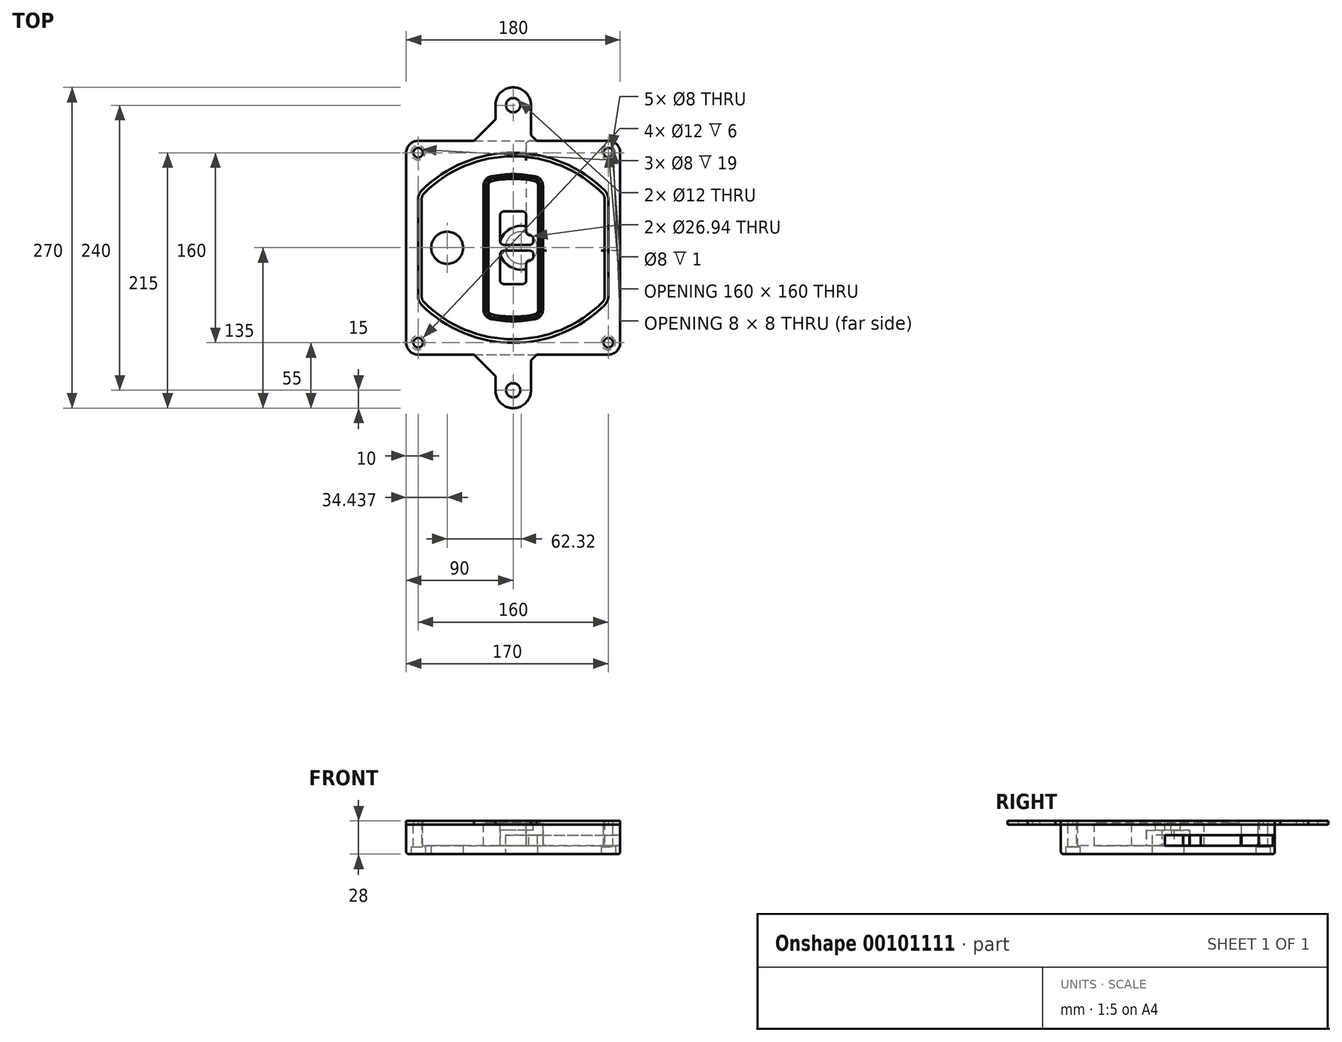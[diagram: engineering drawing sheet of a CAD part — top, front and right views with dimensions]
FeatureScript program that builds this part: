
annotation { "Feature Type Name" : "Feature", "Feature Type Description" : "" }
export const myFeature = defineFeature(function(context is Context, id is Id, definition is map)
    precondition{}
    {
        {
            var Q0;
            Q0=qCreatedBy(makeId("Top.planeOp"),FACE);
            var sketch = newSketch(context, id + "F0", { "sketchPlane" : qUnion([Q0])});
            skPoint(sketch, "E0.rect.middle", {"position": v(0, 0) * mm});
            skLineSegment(sketch, "E1.bottom", {"start": v(-80, -90) * mm, "end": v(80, -90) * mm});
            skLineSegment(sketch, "E1.top", {"start": v(-80, 90) * mm, "end": v(80, 90) * mm});
            skLineSegment(sketch, "E1.left", {"start": v(-90, -80) * mm, "end": v(-90, 80) * mm});
            skLineSegment(sketch, "E1.right", {"start": v(90, -80) * mm, "end": v(90, 80) * mm});
            skLineSegment(sketch, "E2", {"start": v(-90, 90) * mm, "end": v(90, -90) * mm, "construction": true});
            skLineSegment(sketch, "E3", {"start": v(90, 90) * mm, "end": v(-90, -90) * mm, "construction": true});
            skCircle(sketch, "E4", {"center": v(-80, 80) * mm, "radius": 4 * mm});
            skCircle(sketch, "E5", {"center": v(80, 80) * mm, "radius": 4 * mm});
            skCircle(sketch, "E6", {"center": v(80, -80) * mm, "radius": 4 * mm});
            skCircle(sketch, "E7", {"center": v(-80, -80) * mm, "radius": 4 * mm});
            skLineSegment(sketch, "E8", {"start": v(-80, 80) * mm, "end": v(80, 80) * mm, "construction": true});
            skLineSegment(sketch, "E9", {"start": v(80, 80) * mm, "end": v(80, -80) * mm, "construction": true});
            skLineSegment(sketch, "E10", {"start": v(80, -80) * mm, "end": v(-80, -80) * mm, "construction": true});
            skLineSegment(sketch, "E11", {"start": v(-80, -80) * mm, "end": v(-80, 80) * mm, "construction": true});
            skLineSegment(sketch, "E12", {"start": v(-80, 40.98) * mm, "end": v(-80, -40.98) * mm});
            skLineSegment(sketch, "E13", {"start": v(80, 40.98) * mm, "end": v(80, -40.98) * mm});
            skArc(sketch, "E14", {"start": v(77.08, 48.04) * mm, "mid": v(0, 80) * mm, "end": v(-77.08, 48.04) * mm});
            skArc(sketch, "E15", {"start": v(-77.08, -48.04) * mm, "mid": v(0, -80) * mm, "end": v(77.08, -48.04) * mm});
            skLineSegment(sketch, "E16", {"start": v(-80, 0) * mm, "end": v(80, 0) * mm, "construction": true});
            skPoint(sketch, "E17.visualSharp", {"position": v(-80, -45) * mm});
            skArc(sketch, "E17.filletArc", {"start": v(-80, -40.98) * mm, "mid": v(-79.24, -44.8) * mm, "end": v(-77.08, -48.04) * mm});
            skPoint(sketch, "E18.visualSharp", {"position": v(-80, 45) * mm});
            skArc(sketch, "E18.filletArc", {"start": v(-77.08, 48.04) * mm, "mid": v(-79.24, 44.8) * mm, "end": v(-80, 40.98) * mm});
            skPoint(sketch, "E19.visualSharp", {"position": v(80, 45) * mm});
            skArc(sketch, "E19.filletArc", {"start": v(80, 40.98) * mm, "mid": v(79.24, 44.8) * mm, "end": v(77.08, 48.04) * mm});
            skPoint(sketch, "E20.visualSharp", {"position": v(80, -45) * mm});
            skArc(sketch, "E20.filletArc", {"start": v(77.08, -48.04) * mm, "mid": v(79.24, -44.8) * mm, "end": v(80, -40.98) * mm});
            skPoint(sketch, "E21.visualSharp", {"position": v(-90, 90) * mm});
            skArc(sketch, "E21.filletArc", {"start": v(-80, 90) * mm, "mid": v(-87.07, 87.07) * mm, "end": v(-90, 80) * mm});
            skPoint(sketch, "E22.visualSharp", {"position": v(90, 90) * mm});
            skArc(sketch, "E22.filletArc", {"start": v(90, 80) * mm, "mid": v(87.07, 87.07) * mm, "end": v(80, 90) * mm});
            skPoint(sketch, "E23.visualSharp", {"position": v(90, -90) * mm});
            skArc(sketch, "E23.filletArc", {"start": v(80, -90) * mm, "mid": v(87.07, -87.07) * mm, "end": v(90, -80) * mm});
            skPoint(sketch, "E24.visualSharp", {"position": v(-90, -90) * mm});
            skArc(sketch, "E24.filletArc", {"start": v(-90, -80) * mm, "mid": v(-87.07, -87.07) * mm, "end": v(-80, -90) * mm});
            skArc(sketch, "E25.0", {"start": v(77, 40.98) * mm, "mid": v(76.47, 43.65) * mm, "end": v(74.95, 45.92) * mm});
            skLineSegment(sketch, "E25.1", {"start": v(77, 40.98) * mm, "end": v(77, -40.98) * mm});
            skArc(sketch, "E25.2", {"start": v(74.95, -45.92) * mm, "mid": v(76.47, -43.65) * mm, "end": v(77, -40.98) * mm});
            skArc(sketch, "E25.3", {"start": v(-74.95, -45.92) * mm, "mid": v(0, -77) * mm, "end": v(74.95, -45.92) * mm});
            skArc(sketch, "E25.4", {"start": v(-77, -40.98) * mm, "mid": v(-76.47, -43.65) * mm, "end": v(-74.95, -45.92) * mm});
            skArc(sketch, "E25.5", {"start": v(74.95, 45.92) * mm, "mid": v(0, 77) * mm, "end": v(-74.95, 45.92) * mm});
            skLineSegment(sketch, "E25.6", {"start": v(-77, 40.98) * mm, "end": v(-77, -40.98) * mm});
            skArc(sketch, "E25.7", {"start": v(-74.95, 45.92) * mm, "mid": v(-76.47, 43.65) * mm, "end": v(-77, 40.98) * mm});
            skArc(sketch, "E26.0", {"start": v(-79.9, 50.87) * mm, "mid": v(-82.94, 46.33) * mm, "end": v(-84, 40.98) * mm});
            skArc(sketch, "E26.1", {"start": v(79.9, 50.87) * mm, "mid": v(0, 84) * mm, "end": v(-79.9, 50.87) * mm});
            skArc(sketch, "E26.2", {"start": v(84, 40.98) * mm, "mid": v(82.94, 46.33) * mm, "end": v(79.9, 50.87) * mm});
            skLineSegment(sketch, "E26.3", {"start": v(84, 40.98) * mm, "end": v(84, -40.98) * mm});
            skArc(sketch, "E26.4", {"start": v(79.9, -50.87) * mm, "mid": v(82.94, -46.33) * mm, "end": v(84, -40.98) * mm});
            skLineSegment(sketch, "E26.5", {"start": v(-84, 40.98) * mm, "end": v(-84, -40.98) * mm});
            skArc(sketch, "E26.6", {"start": v(-79.9, -50.87) * mm, "mid": v(0, -84) * mm, "end": v(79.9, -50.87) * mm});
            skArc(sketch, "E26.7", {"start": v(-84, -40.98) * mm, "mid": v(-82.94, -46.33) * mm, "end": v(-79.9, -50.87) * mm});
            skSolve(sketch);
        }
        {
            var Q0;
            Q0=makeQuery(id+"F0.imprint","IMPRINT",FACE,{"disambiguationData":[TD([[makeQuery(id+"F0.imprint","IMPRINT",EDGE,{"derivedFrom":sQuery(id+"F0.wireOp",EDGE,"E1.bottom")}),1.0]])]});
            var Q1;
            Q1=makeQuery(id+"F0.imprint","IMPRINT",FACE,{"disambiguationData":[TD([[makeQuery(id+"F0.imprint","IMPRINT",EDGE,{"derivedFrom":sQuery(id+"F0.wireOp",EDGE,"E12")}),1.0]])]});
            var Q2;
            Q2=makeQuery(id+"F0.imprint","IMPRINT",FACE,{"disambiguationData":[TD([[makeQuery(id+"F0.imprint","IMPRINT",EDGE,{"derivedFrom":sQuery(id+"F0.wireOp",EDGE,"E25.0")}),1.0]])]});
            var Q3;
            Q3=makeQuery(id+"F0.imprint","IMPRINT",FACE,{"disambiguationData":[TD([[makeQuery(id+"F0.imprint","IMPRINT",EDGE,{"derivedFrom":sQuery(id+"F0.wireOp",EDGE,"E12")}),-1.0]])]});
            extrude(context, id + "F1", {"entities" : qUnion([Q0, Q1, Q2, Q3]), "oppositeDirection" : true, "depth" : 25 * mm});
        }
        {
            var Q0;
            Q0=makeQuery(id+"F0.imprint","IMPRINT",FACE,{"disambiguationData":[TD([[makeQuery(id+"F0.imprint","IMPRINT",EDGE,{"derivedFrom":sQuery(id+"F0.wireOp",EDGE,"E12")}),1.0]])]});
            extrude(context, id + "F2", {"entities" : qUnion([Q0]), "operationType" : NewBodyOperationType.ADD, "depth" : 3 * mm});
        }
        {
            var Q0;
            Q0=makeQuery(id+"F0.imprint","IMPRINT",FACE,{"disambiguationData":[TD([[makeQuery(id+"F0.imprint","IMPRINT",EDGE,{"derivedFrom":sQuery(id+"F0.wireOp",EDGE,"E25.0")}),1.0]])]});
            extrude(context, id + "F3", {"entities" : qUnion([Q0]), "operationType" : NewBodyOperationType.REMOVE, "oppositeDirection" : true, "depth" : 18 * mm});
        }
        {
            var Q0;
            Q0=makeQuery(id+"F2.opExtrude","CAP_FACE",FACE,{"disambiguationData":[OSD([sQuery(id+"F0.wireOp",EDGE,"E12"),sQuery(id+"F0.wireOp",EDGE,"E13"),sQuery(id+"F0.wireOp",EDGE,"E14"),sQuery(id+"F0.wireOp",EDGE,"E15"),sQuery(id+"F0.wireOp",EDGE,"E17.filletArc"),sQuery(id+"F0.wireOp",EDGE,"E18.filletArc"),sQuery(id+"F0.wireOp",EDGE,"E19.filletArc"),sQuery(id+"F0.wireOp",EDGE,"E20.filletArc"),sQuery(id+"F0.wireOp",EDGE,"E25.0"),sQuery(id+"F0.wireOp",EDGE,"E25.1"),sQuery(id+"F0.wireOp",EDGE,"E25.2"),sQuery(id+"F0.wireOp",EDGE,"E25.3"),sQuery(id+"F0.wireOp",EDGE,"E25.4"),sQuery(id+"F0.wireOp",EDGE,"E25.5"),sQuery(id+"F0.wireOp",EDGE,"E25.6"),sQuery(id+"F0.wireOp",EDGE,"E25.7")])],"isStart":false});
            var sketch = newSketch(context, id + "F4", { "sketchPlane" : qUnion([Q0])});
            skArc(sketch, "E27.0", {"start": v(-18.64, -60.07) * mm, "mid": v(0, -62) * mm, "end": v(18.64, -60.07) * mm});
            skArc(sketch, "E28.0", {"start": v(18.64, 60.07) * mm, "mid": v(0, 62) * mm, "end": v(-18.64, 60.07) * mm});
            skLineSegment(sketch, "E29", {"start": v(-25, 52.24) * mm, "end": v(-25, -52.24) * mm});
            skLineSegment(sketch, "E30", {"start": v(25, 52.24) * mm, "end": v(25, -52.24) * mm});
            skLineSegment(sketch, "E31", {"start": v(-25, 58.5) * mm, "end": v(25, 58.5) * mm, "construction": true});
            skLineSegment(sketch, "E32", {"start": v(-25, -58.5) * mm, "end": v(25, -58.5) * mm, "construction": true});
            skPoint(sketch, "E33.visualSharp", {"position": v(-25, 58.5) * mm});
            skArc(sketch, "E33.filletArc", {"start": v(-18.64, 60.07) * mm, "mid": v(-23.2, 57.28) * mm, "end": v(-25, 52.24) * mm});
            skPoint(sketch, "E34.visualSharp", {"position": v(25, 58.5) * mm});
            skArc(sketch, "E34.filletArc", {"start": v(25, 52.24) * mm, "mid": v(23.2, 57.28) * mm, "end": v(18.64, 60.07) * mm});
            skPoint(sketch, "E35.visualSharp", {"position": v(25, -58.5) * mm});
            skArc(sketch, "E35.filletArc", {"start": v(18.64, -60.07) * mm, "mid": v(23.2, -57.28) * mm, "end": v(25, -52.24) * mm});
            skPoint(sketch, "E36.visualSharp", {"position": v(-25, -58.5) * mm});
            skArc(sketch, "E36.filletArc", {"start": v(-25, -52.24) * mm, "mid": v(-23.2, -57.28) * mm, "end": v(-18.64, -60.07) * mm});
            skArc(sketch, "E37.0", {"start": v(74.95, 45.92) * mm, "mid": v(0, 77) * mm, "end": v(-74.95, 45.92) * mm});
            skArc(sketch, "E37.1", {"start": v(-74.95, 45.92) * mm, "mid": v(-76.47, 43.65) * mm, "end": v(-77, 40.98) * mm});
            skLineSegment(sketch, "E37.2", {"start": v(-77, 40.98) * mm, "end": v(-77, -40.98) * mm});
            skArc(sketch, "E37.3", {"start": v(-77, -40.98) * mm, "mid": v(-76.47, -43.65) * mm, "end": v(-74.95, -45.92) * mm});
            skArc(sketch, "E37.4", {"start": v(-74.95, -45.92) * mm, "mid": v(0, -77) * mm, "end": v(74.95, -45.92) * mm});
            skArc(sketch, "E37.5", {"start": v(74.95, -45.92) * mm, "mid": v(76.47, -43.65) * mm, "end": v(77, -40.98) * mm});
            skLineSegment(sketch, "E37.6", {"start": v(77, 40.98) * mm, "end": v(77, -40.98) * mm});
            skArc(sketch, "E37.7", {"start": v(77, 40.98) * mm, "mid": v(76.47, 43.65) * mm, "end": v(74.95, 45.92) * mm});
            skLineSegment(sketch, "E38.0", {"start": v(23, 52.24) * mm, "end": v(23, -52.24) * mm});
            skArc(sketch, "E38.1", {"start": v(18.23, -58.11) * mm, "mid": v(21.66, -56.02) * mm, "end": v(23, -52.24) * mm});
            skArc(sketch, "E38.2", {"start": v(-18.23, -58.11) * mm, "mid": v(0, -60) * mm, "end": v(18.23, -58.11) * mm});
            skArc(sketch, "E38.3", {"start": v(-23, -52.24) * mm, "mid": v(-21.66, -56.02) * mm, "end": v(-18.23, -58.11) * mm});
            skLineSegment(sketch, "E38.4", {"start": v(-23, 52.24) * mm, "end": v(-23, -52.24) * mm});
            skArc(sketch, "E38.5", {"start": v(23, 52.24) * mm, "mid": v(21.66, 56.02) * mm, "end": v(18.23, 58.11) * mm});
            skArc(sketch, "E38.6", {"start": v(-18.23, 58.11) * mm, "mid": v(-21.66, 56.02) * mm, "end": v(-23, 52.24) * mm});
            skArc(sketch, "E38.7", {"start": v(18.23, 58.11) * mm, "mid": v(0, 60) * mm, "end": v(-18.23, 58.11) * mm});
            skArc(sketch, "E39.0", {"start": v(21, 52.24) * mm, "mid": v(20.1, 54.76) * mm, "end": v(17.82, 56.15) * mm});
            skLineSegment(sketch, "E39.1", {"start": v(21, 52.24) * mm, "end": v(21, -52.24) * mm});
            skArc(sketch, "E39.2", {"start": v(17.82, -56.15) * mm, "mid": v(20.1, -54.76) * mm, "end": v(21, -52.24) * mm});
            skArc(sketch, "E39.3", {"start": v(-17.82, -56.15) * mm, "mid": v(0, -58) * mm, "end": v(17.82, -56.15) * mm});
            skArc(sketch, "E39.4", {"start": v(-21, -52.24) * mm, "mid": v(-20.1, -54.76) * mm, "end": v(-17.82, -56.15) * mm});
            skArc(sketch, "E39.5", {"start": v(17.82, 56.15) * mm, "mid": v(0, 58) * mm, "end": v(-17.82, 56.15) * mm});
            skLineSegment(sketch, "E39.6", {"start": v(-21, 52.24) * mm, "end": v(-21, -52.24) * mm});
            skArc(sketch, "E39.7", {"start": v(-17.82, 56.15) * mm, "mid": v(-20.1, 54.76) * mm, "end": v(-21, 52.24) * mm});
            skLineSegment(sketch, "E40", {"start": v(-25, 0) * mm, "end": v(25, 0) * mm, "construction": true});
            skLineSegment(sketch, "E41", {"start": v(-11, 5.5) * mm, "end": v(-11, 27.5) * mm});
            skLineSegment(sketch, "E42", {"start": v(-8, 30.5) * mm, "end": v(8, 30.5) * mm});
            skLineSegment(sketch, "E43", {"start": v(11, 27.5) * mm, "end": v(11, 13.5) * mm});
            skLineSegment(sketch, "E44", {"start": v(14, 10.5) * mm, "end": v(14, 10.5) * mm});
            skLineSegment(sketch, "E45", {"start": v(17, 7.5) * mm, "end": v(17, 5.5) * mm});
            skLineSegment(sketch, "E46", {"start": v(14, 2.5) * mm, "end": v(-8, 2.5) * mm});
            skPoint(sketch, "E47.visualSharp", {"position": v(-11, 30.5) * mm});
            skArc(sketch, "E47.filletArc", {"start": v(-8, 30.5) * mm, "mid": v(-10.12, 29.62) * mm, "end": v(-11, 27.5) * mm});
            skPoint(sketch, "E48.visualSharp", {"position": v(11, 30.5) * mm});
            skArc(sketch, "E48.filletArc", {"start": v(11, 27.5) * mm, "mid": v(10.12, 29.62) * mm, "end": v(8, 30.5) * mm});
            skPoint(sketch, "E49.visualSharp", {"position": v(11, 10.5) * mm});
            skArc(sketch, "E49.filletArc", {"start": v(11, 13.5) * mm, "mid": v(11.88, 11.38) * mm, "end": v(14, 10.5) * mm});
            skPoint(sketch, "E50.visualSharp", {"position": v(17, 10.5) * mm});
            skArc(sketch, "E50.filletArc", {"start": v(17, 7.5) * mm, "mid": v(16.12, 9.62) * mm, "end": v(14, 10.5) * mm});
            skPoint(sketch, "E51.visualSharp", {"position": v(17, 2.5) * mm});
            skArc(sketch, "E51.filletArc", {"start": v(14, 2.5) * mm, "mid": v(16.12, 3.38) * mm, "end": v(17, 5.5) * mm});
            skPoint(sketch, "E52.visualSharp", {"position": v(-11, 2.5) * mm});
            skArc(sketch, "E52.filletArc", {"start": v(-11, 5.5) * mm, "mid": v(-10.12, 3.38) * mm, "end": v(-8, 2.5) * mm});
            skLineSegment(sketch, "E53.0.MirrorCS", {"start": v(14, -2.5) * mm, "end": v(-8, -2.5) * mm});
            skArc(sketch, "E54.0.MirrorCS", {"start": v(-11, -5.5) * mm, "mid": v(-10.12, -3.38) * mm, "end": v(-8, -2.5) * mm});
            skLineSegment(sketch, "E55.0.MirrorCS", {"start": v(-11, -5.5) * mm, "end": v(-11, -27.5) * mm});
            skArc(sketch, "E56.0.MirrorCS", {"start": v(-8, -30.5) * mm, "mid": v(-10.12, -29.62) * mm, "end": v(-11, -27.5) * mm});
            skLineSegment(sketch, "E57.0.MirrorCS", {"start": v(-8, -30.5) * mm, "end": v(8, -30.5) * mm});
            skArc(sketch, "E58.0.MirrorCS", {"start": v(11, -27.5) * mm, "mid": v(10.12, -29.62) * mm, "end": v(8, -30.5) * mm});
            skLineSegment(sketch, "E59.0.MirrorCS", {"start": v(11, -27.5) * mm, "end": v(11, -13.5) * mm});
            skArc(sketch, "E60.0.MirrorCS", {"start": v(11, -13.5) * mm, "mid": v(11.88, -11.38) * mm, "end": v(14, -10.5) * mm});
            skArc(sketch, "E61.0.MirrorCS", {"start": v(17, -7.5) * mm, "mid": v(16.12, -9.62) * mm, "end": v(14, -10.5) * mm});
            skLineSegment(sketch, "E62.0.MirrorCS", {"start": v(17, -7.5) * mm, "end": v(17, -5.5) * mm});
            skArc(sketch, "E63.0.MirrorCS", {"start": v(14, -2.5) * mm, "mid": v(16.12, -3.38) * mm, "end": v(17, -5.5) * mm});
            skSolve(sketch);
        }
        {
            var Q0;
            Q0=makeQuery(id+"F4.imprint","IMPRINT",FACE,{"disambiguationData":[TD([[makeQuery(id+"F4.imprint","IMPRINT",EDGE,{"derivedFrom":sQuery(id+"F4.wireOp",EDGE,"E27.0")}),1.0]])]});
            var Q1;
            Q1=makeQuery(id+"F4.imprint","IMPRINT",FACE,{"disambiguationData":[TD([[makeQuery(id+"F4.imprint","IMPRINT",EDGE,{"derivedFrom":sQuery(id+"F4.wireOp",EDGE,"E38.0")}),-1.0]])]});
            var Q2;
            Q2=makeQuery(id+"F4.imprint","IMPRINT",FACE,{"disambiguationData":[TD([[makeQuery(id+"F4.imprint","IMPRINT",EDGE,{"derivedFrom":sQuery(id+"F4.wireOp",EDGE,"E39.0")}),1.0]])]});
            extrude(context, id + "F5", {"entities" : qUnion([Q0, Q1, Q2]), "operationType" : NewBodyOperationType.ADD, "endBound" : BoundingType.UP_TO_NEXT, "oppositeDirection" : true, "depth" : 25 * mm});
        }
        {
            var Q0;
            Q0=makeQuery(id+"F4.imprint","IMPRINT",FACE,{"disambiguationData":[TD([[makeQuery(id+"F4.imprint","IMPRINT",EDGE,{"derivedFrom":sQuery(id+"F4.wireOp",EDGE,"E38.0")}),-1.0]])]});
            extrude(context, id + "F6", {"entities" : qUnion([Q0]), "operationType" : NewBodyOperationType.REMOVE, "oppositeDirection" : true, "depth" : 2 * mm});
        }
        {
            var Q0;
            Q0=makeQuery(id+"F1.opExtrude","CAP_FACE",FACE,{"disambiguationData":[OSD([sQuery(id+"F0.wireOp",EDGE,"E1.bottom"),sQuery(id+"F0.wireOp",EDGE,"E1.top"),sQuery(id+"F0.wireOp",EDGE,"E1.left"),sQuery(id+"F0.wireOp",EDGE,"E1.right"),sQuery(id+"F0.wireOp",EDGE,"E4"),sQuery(id+"F0.wireOp",EDGE,"E5"),sQuery(id+"F0.wireOp",EDGE,"E6"),sQuery(id+"F0.wireOp",EDGE,"E7"),sQuery(id+"F0.wireOp",EDGE,"E21.filletArc"),sQuery(id+"F0.wireOp",EDGE,"E22.filletArc"),sQuery(id+"F0.wireOp",EDGE,"E23.filletArc"),sQuery(id+"F0.wireOp",EDGE,"E24.filletArc")])],"isStart":false});
            var sketch = newSketch(context, id + "F7", { "sketchPlane" : qUnion([Q0])});
            skCircle(sketch, "E64", {"center": v(6.76, 0) * mm, "radius": 13.47 * mm});
            skCircle(sketch, "E65", {"center": v(-55.56, 0) * mm, "radius": 13.47 * mm});
            skLineSegment(sketch, "E66", {"start": v(90, 0) * mm, "end": v(-90, 0) * mm});
            skCircle(sketch, "E67", {"center": v(6.76, 0) * mm, "radius": 18.47 * mm});
            skCircle(sketch, "E68", {"center": v(80, -80) * mm, "radius": 6 * mm});
            skCircle(sketch, "E69", {"center": v(-80, -80) * mm, "radius": 6 * mm});
            skCircle(sketch, "E70", {"center": v(-80, 80) * mm, "radius": 6 * mm});
            skCircle(sketch, "E71", {"center": v(80, 80) * mm, "radius": 6 * mm});
            skSolve(sketch);
        }
        {
            var Q0;
            {var subQ1=sQuery(id+"F7.wireOp",EDGE,"E66");var subQ4=sQuery(id+"F7.wireOp",EDGE,"E64");var subQ6=makeQuery(id+"F7.imprint","INTERSECT",VERTEX,{"disambiguationData":[OD(0.0)],"derivedFrom":[subQ4,subQ1]});Q0=makeQuery(id+"F7.imprint","IMPRINT",FACE,{"disambiguationData":[TD([[makeQuery(id+"F7.imprint","IMPRINT",EDGE,{"disambiguationData":[TD([[subQ6,-1.0]])],"derivedFrom":subQ4}),-1.0]])]});}
            var Q1;
            {var subQ0=sQuery(id+"F7.wireOp",EDGE,"E66");var subQ1=sQuery(id+"F7.wireOp",EDGE,"E64");var subQ3=makeQuery(id+"F7.imprint","INTERSECT",VERTEX,{"disambiguationData":[OD(0.0)],"derivedFrom":[subQ1,subQ0]});Q1=makeQuery(id+"F7.imprint","IMPRINT",FACE,{"disambiguationData":[TD([[makeQuery(id+"F7.imprint","IMPRINT",EDGE,{"disambiguationData":[TD([[subQ3,-1.0]])],"derivedFrom":subQ1}),1.0]])]});}
            var Q2;
            {var subQ0=sQuery(id+"F7.wireOp",EDGE,"E66");var subQ1=sQuery(id+"F7.wireOp",EDGE,"E64");var subQ3=makeQuery(id+"F7.imprint","INTERSECT",VERTEX,{"disambiguationData":[OD(0.0)],"derivedFrom":[subQ1,subQ0]});Q2=makeQuery(id+"F7.imprint","IMPRINT",FACE,{"disambiguationData":[TD([[makeQuery(id+"F7.imprint","IMPRINT",EDGE,{"disambiguationData":[TD([[subQ3,1.0]])],"derivedFrom":subQ1}),1.0]])]});}
            var Q3;
            {var subQ1=sQuery(id+"F7.wireOp",EDGE,"E66");var subQ4=sQuery(id+"F7.wireOp",EDGE,"E64");var subQ6=makeQuery(id+"F7.imprint","INTERSECT",VERTEX,{"disambiguationData":[OD(0.0)],"derivedFrom":[subQ4,subQ1]});Q3=makeQuery(id+"F7.imprint","IMPRINT",FACE,{"disambiguationData":[TD([[makeQuery(id+"F7.imprint","IMPRINT",EDGE,{"disambiguationData":[TD([[subQ6,1.0]])],"derivedFrom":subQ4}),-1.0]])]});}
            extrude(context, id + "F8", {"entities" : qUnion([Q0, Q1, Q2, Q3]), "operationType" : NewBodyOperationType.ADD, "oppositeDirection" : true, "depth" : 20 * mm});
        }
        {
            var Q0;
            {var subQ0=sQuery(id+"F7.wireOp",EDGE,"E66");var subQ1=sQuery(id+"F7.wireOp",EDGE,"E64");var subQ3=makeQuery(id+"F7.imprint","INTERSECT",VERTEX,{"disambiguationData":[OD(0.0)],"derivedFrom":[subQ1,subQ0]});Q0=makeQuery(id+"F7.imprint","IMPRINT",FACE,{"disambiguationData":[TD([[makeQuery(id+"F7.imprint","IMPRINT",EDGE,{"disambiguationData":[TD([[subQ3,-1.0]])],"derivedFrom":subQ1}),1.0]])]});}
            var Q1;
            {var subQ0=sQuery(id+"F7.wireOp",EDGE,"E66");var subQ1=sQuery(id+"F7.wireOp",EDGE,"E64");var subQ3=makeQuery(id+"F7.imprint","INTERSECT",VERTEX,{"disambiguationData":[OD(0.0)],"derivedFrom":[subQ1,subQ0]});Q1=makeQuery(id+"F7.imprint","IMPRINT",FACE,{"disambiguationData":[TD([[makeQuery(id+"F7.imprint","IMPRINT",EDGE,{"disambiguationData":[TD([[subQ3,1.0]])],"derivedFrom":subQ1}),1.0]])]});}
            extrude(context, id + "F9", {"entities" : qUnion([Q0, Q1]), "operationType" : NewBodyOperationType.REMOVE, "oppositeDirection" : true, "depth" : 16 * mm});
        }
        {
            var Q0;
            {var subQ0=sQuery(id+"F7.wireOp",EDGE,"E66");var subQ1=sQuery(id+"F7.wireOp",EDGE,"E65");var subQ3=makeQuery(id+"F7.imprint","INTERSECT",VERTEX,{"disambiguationData":[OD(0.0)],"derivedFrom":[subQ1,subQ0]});Q0=makeQuery(id+"F7.imprint","IMPRINT",FACE,{"disambiguationData":[TD([[makeQuery(id+"F7.imprint","IMPRINT",EDGE,{"disambiguationData":[TD([[subQ3,-1.0]])],"derivedFrom":subQ1}),1.0]])]});}
            var Q1;
            {var subQ0=sQuery(id+"F7.wireOp",EDGE,"E66");var subQ1=sQuery(id+"F7.wireOp",EDGE,"E65");var subQ3=makeQuery(id+"F7.imprint","INTERSECT",VERTEX,{"disambiguationData":[OD(0.0)],"derivedFrom":[subQ1,subQ0]});Q1=makeQuery(id+"F7.imprint","IMPRINT",FACE,{"disambiguationData":[TD([[makeQuery(id+"F7.imprint","IMPRINT",EDGE,{"disambiguationData":[TD([[subQ3,1.0]])],"derivedFrom":subQ1}),1.0]])]});}
            extrude(context, id + "F10", {"entities" : qUnion([Q0, Q1]), "operationType" : NewBodyOperationType.REMOVE, "oppositeDirection" : true, "depth" : 25 * mm});
        }
        {
            var Q0;
            Q0=makeQuery(id+"F7.imprint","IMPRINT",FACE,{"disambiguationData":[TD([[makeQuery(id+"F7.imprint","IMPRINT",EDGE,{"derivedFrom":sQuery(id+"F7.wireOp",EDGE,"E68")}),1.0]])]});
            var Q1;
            Q1=makeQuery(id+"F7.imprint","IMPRINT",FACE,{"disambiguationData":[TD([[makeQuery(id+"F7.imprint","IMPRINT",EDGE,{"derivedFrom":makeQuery(id+"F1.opExtrude","CAP_EDGE",EDGE,{"disambiguationData":[OSD([sQuery(id+"F0.wireOp",EDGE,"E5")])],"isStart":false})}),-1.0]])]});
            var Q2;
            Q2=makeQuery(id+"F7.imprint","IMPRINT",FACE,{"disambiguationData":[TD([[makeQuery(id+"F7.imprint","IMPRINT",EDGE,{"derivedFrom":sQuery(id+"F7.wireOp",EDGE,"E69")}),1.0]])]});
            var Q3;
            Q3=makeQuery(id+"F7.imprint","IMPRINT",FACE,{"disambiguationData":[TD([[makeQuery(id+"F7.imprint","IMPRINT",EDGE,{"derivedFrom":makeQuery(id+"F1.opExtrude","CAP_EDGE",EDGE,{"disambiguationData":[OSD([sQuery(id+"F0.wireOp",EDGE,"E4")])],"isStart":false})}),-1.0]])]});
            var Q4;
            Q4=makeQuery(id+"F7.imprint","IMPRINT",FACE,{"disambiguationData":[TD([[makeQuery(id+"F7.imprint","IMPRINT",EDGE,{"derivedFrom":sQuery(id+"F7.wireOp",EDGE,"E70")}),1.0]])]});
            var Q5;
            Q5=makeQuery(id+"F7.imprint","IMPRINT",FACE,{"disambiguationData":[TD([[makeQuery(id+"F7.imprint","IMPRINT",EDGE,{"derivedFrom":makeQuery(id+"F1.opExtrude","CAP_EDGE",EDGE,{"disambiguationData":[OSD([sQuery(id+"F0.wireOp",EDGE,"E7")])],"isStart":false})}),-1.0]])]});
            var Q6;
            Q6=makeQuery(id+"F7.imprint","IMPRINT",FACE,{"disambiguationData":[TD([[makeQuery(id+"F7.imprint","IMPRINT",EDGE,{"derivedFrom":sQuery(id+"F7.wireOp",EDGE,"E71")}),1.0]])]});
            var Q7;
            Q7=makeQuery(id+"F7.imprint","IMPRINT",FACE,{"disambiguationData":[TD([[makeQuery(id+"F7.imprint","IMPRINT",EDGE,{"derivedFrom":makeQuery(id+"F1.opExtrude","CAP_EDGE",EDGE,{"disambiguationData":[OSD([sQuery(id+"F0.wireOp",EDGE,"E6")])],"isStart":false})}),-1.0]])]});
            extrude(context, id + "F11", {"entities" : qUnion([Q0, Q1, Q2, Q3, Q4, Q5, Q6, Q7]), "operationType" : NewBodyOperationType.REMOVE, "oppositeDirection" : true, "depth" : 6 * mm});
        }
        {
            var Q0;
            Q0=makeQuery(id+"F9.boolean.opBoolean","COPY",FACE,{"derivedFrom":makeQuery(id+"F9.opExtrude","CAP_FACE",FACE,{"disambiguationData":[OSD([sQuery(id+"F7.wireOp",EDGE,"E64")])],"isStart":false})});
            var sketch = newSketch(context, id + "F12", { "sketchPlane" : qUnion([Q0])});
            skArc(sketch, "E72.0", {"start": v(11, -88.19) * mm, "mid": v(97.1, -83.6) * mm, "end": v(92.5, 2.5) * mm});
            skLineSegment(sketch, "E72.1", {"start": v(11, -17.97) * mm, "end": v(11, -17.97) * mm});
            skLineSegment(sketch, "E73", {"start": v(92.5, -105.13) * mm, "end": v(102.3, -105.13) * mm});
            skLineSegment(sketch, "E74.0", {"start": v(92.5, 2.5) * mm, "end": v(14, 2.5) * mm});
            skArc(sketch, "E74.1", {"start": v(14, 2.5) * mm, "mid": v(16.12, 3.38) * mm, "end": v(17, 5.5) * mm});
            skLineSegment(sketch, "E74.2", {"start": v(17, 7.5) * mm, "end": v(17, 5.5) * mm});
            skArc(sketch, "E74.3", {"start": v(17, 7.5) * mm, "mid": v(16.12, 9.62) * mm, "end": v(14, 10.5) * mm});
            skArc(sketch, "E74.4", {"start": v(11, 13.5) * mm, "mid": v(11.88, 11.38) * mm, "end": v(14, 10.5) * mm});
            skLineSegment(sketch, "E74.5", {"start": v(11, 13.5) * mm, "end": v(11, -88.19) * mm});
            skLineSegment(sketch, "E74.7", {"start": v(92.5, -2.5) * mm, "end": v(14, -2.5) * mm});
            skArc(sketch, "E74.8", {"start": v(14, -2.5) * mm, "mid": v(16.12, -3.38) * mm, "end": v(17, -5.5) * mm});
            skLineSegment(sketch, "E74.9", {"start": v(17, -7.5) * mm, "end": v(17, -5.5) * mm});
            skArc(sketch, "E74.10", {"start": v(17, -7.5) * mm, "mid": v(16.12, -9.62) * mm, "end": v(14, -10.5) * mm});
            skArc(sketch, "E74.11", {"start": v(11, -13.5) * mm, "mid": v(11.88, -11.38) * mm, "end": v(14, -10.5) * mm});
            skLineSegment(sketch, "E74.12", {"start": v(11, -17.97) * mm, "end": v(11, -13.5) * mm});
            skPoint(sketch, "E75.orphan", {"position": v(11, -27.5) * mm});
            skPoint(sketch, "E76.orphan", {"position": v(-8, -2.5) * mm});
            skPoint(sketch, "E77.orphan", {"position": v(-8, 2.5) * mm});
            skPoint(sketch, "E78.orphan", {"position": v(11, 27.5) * mm});
            skSolve(sketch);
        }
        {
            var Q0;
            {var subQ7=sQuery(id+"F12.wireOp",EDGE,"E72.0");var subQ14=sQuery(id+"F12.wireOp",EDGE,"E72.1");var subQ16=sQuery(id+"F12.wireOp",EDGE,"E74.1");var subQ18=sQuery(id+"F12.wireOp",EDGE,"E74.8");Q0=qUnion([makeQuery(id+"F12.imprint","IMPRINT",FACE,{"disambiguationData":[TD([[makeQuery(id+"F12.imprint","IMPRINT",EDGE,{"derivedFrom":subQ7}),1.0]])]}),makeQuery(id+"F12.imprint","IMPRINT",FACE,{"disambiguationData":[TD([[makeQuery(id+"F12.imprint","IMPRINT",EDGE,{"derivedFrom":subQ14}),1.0]])]}),makeQuery(id+"F12.imprint","IMPRINT",FACE,{"disambiguationData":[TD([[makeQuery(id+"F12.imprint","IMPRINT",EDGE,{"derivedFrom":subQ16}),1.0]])]}),makeQuery(id+"F12.imprint","IMPRINT",FACE,{"disambiguationData":[TD([[makeQuery(id+"F12.imprint","IMPRINT",EDGE,{"derivedFrom":subQ18}),-1.0]])]})]);}
            var Q1;
            Q1=makeQuery(id+"F5.boolean.opBoolean","SPLIT",FACE,{"disambiguationData":[TD([makeQuery(id+"F5.opExtrude","SWEPT_FACE",FACE,{"disambiguationData":[OSD([sQuery(id+"F4.wireOp",EDGE,"E41")])]})])],"derivedFrom":makeQuery(id+"F3.boolean.opBoolean","COPY",FACE,{"derivedFrom":makeQuery(id+"F3.opExtrude","CAP_FACE",FACE,{"disambiguationData":[OSD([sQuery(id+"F0.wireOp",EDGE,"E25.0"),sQuery(id+"F0.wireOp",EDGE,"E25.1"),sQuery(id+"F0.wireOp",EDGE,"E25.2"),sQuery(id+"F0.wireOp",EDGE,"E25.3"),sQuery(id+"F0.wireOp",EDGE,"E25.4"),sQuery(id+"F0.wireOp",EDGE,"E25.5"),sQuery(id+"F0.wireOp",EDGE,"E25.6"),sQuery(id+"F0.wireOp",EDGE,"E25.7")])],"isStart":false})})});
            extrude(context, id + "F13", {"entities" : qUnion([Q0]), "operationType" : NewBodyOperationType.REMOVE, "endBound" : BoundingType.UP_TO_SURFACE, "endBoundEntityFace" : qUnion([Q1]), "depth" : 25 * mm});
        }
        {
            var Q0;
            Q0=makeQuery(id+"F3.boolean.opBoolean","COPY",EDGE,{"derivedFrom":makeQuery(id+"F3.opExtrude","CAP_EDGE",EDGE,{"disambiguationData":[OSD([sQuery(id+"F0.wireOp",EDGE,"E25.6")])],"isStart":false})});
            var Q1;
            Q1=makeQuery(id+"F8.boolean.opBoolean","INTERSECT",EDGE,{"derivedFrom":[makeQuery(id+"F5.opExtrude","SWEPT_FACE",FACE,{"disambiguationData":[OSD([sQuery(id+"F4.wireOp",EDGE,"E30")])]}),makeQuery(id+"F8.opExtrude","CAP_FACE",FACE,{"disambiguationData":[OSD([sQuery(id+"F7.wireOp",EDGE,"E67")])],"isStart":false})]});
            var Q2;
            Q2=makeQuery(id+"F8.boolean.opBoolean","INTERSECT",EDGE,{"disambiguationData":[OD(1.0)],"derivedFrom":[makeQuery(id+"F5.opExtrude","SWEPT_FACE",FACE,{"disambiguationData":[OSD([sQuery(id+"F4.wireOp",EDGE,"E30")])]}),makeQuery(id+"F8.opExtrude","SWEPT_FACE",FACE,{"disambiguationData":[OSD([sQuery(id+"F7.wireOp",EDGE,"E67")])]})]});
            var Q3;
            {var subQ0=makeQuery(id+"F3.boolean.opBoolean","COPY",FACE,{"derivedFrom":makeQuery(id+"F3.opExtrude","CAP_FACE",FACE,{"disambiguationData":[OSD([sQuery(id+"F0.wireOp",EDGE,"E25.0"),sQuery(id+"F0.wireOp",EDGE,"E25.1"),sQuery(id+"F0.wireOp",EDGE,"E25.2"),sQuery(id+"F0.wireOp",EDGE,"E25.3"),sQuery(id+"F0.wireOp",EDGE,"E25.4"),sQuery(id+"F0.wireOp",EDGE,"E25.5"),sQuery(id+"F0.wireOp",EDGE,"E25.6"),sQuery(id+"F0.wireOp",EDGE,"E25.7")])],"isStart":false})});var subQ1=sQuery(id+"F4.wireOp",EDGE,"E30");Q3=makeQuery(id+"F8.boolean.opBoolean","SPLIT",EDGE,{"disambiguationData":[TD([makeQuery(id+"F5.opExtrude","SWEPT_FACE",FACE,{"disambiguationData":[OSD([sQuery(id+"F4.wireOp",EDGE,"E35.filletArc")])]})])],"derivedFrom":makeQuery(id+"F5.opExtrude","TWEAK_EDGE",EDGE,{"derivedFrom":[subQ0,makeQuery(id+"F4.imprint","IMPRINT",EDGE,{"derivedFrom":subQ1})]})});}
            var Q4;
            {var subQ0=sQuery(id+"F0.wireOp",EDGE,"E25.0");var subQ1=sQuery(id+"F0.wireOp",EDGE,"E25.1");var subQ2=sQuery(id+"F0.wireOp",EDGE,"E25.2");var subQ3=sQuery(id+"F0.wireOp",EDGE,"E25.3");var subQ4=sQuery(id+"F0.wireOp",EDGE,"E25.4");var subQ5=sQuery(id+"F0.wireOp",EDGE,"E25.5");var subQ6=sQuery(id+"F0.wireOp",EDGE,"E25.6");var subQ7=sQuery(id+"F0.wireOp",EDGE,"E25.7");Q4=makeQuery(id+"F8.boolean.opBoolean","INTERSECT",EDGE,{"derivedFrom":[makeQuery(id+"F5.boolean.opBoolean","SPLIT",FACE,{"disambiguationData":[TD([makeQuery(id+"F2.opExtrude","SWEPT_FACE",FACE,{"disambiguationData":[OSD([subQ0])]})])],"derivedFrom":makeQuery(id+"F3.boolean.opBoolean","COPY",FACE,{"derivedFrom":makeQuery(id+"F3.opExtrude","CAP_FACE",FACE,{"disambiguationData":[OSD([subQ0,subQ1,subQ2,subQ3,subQ4,subQ5,subQ6,subQ7])],"isStart":false})})}),makeQuery(id+"F8.opExtrude","SWEPT_FACE",FACE,{"disambiguationData":[OSD([sQuery(id+"F7.wireOp",EDGE,"E67")])]})]});}
            var Q5;
            Q5=makeQuery(id+"F8.boolean.opBoolean","INTERSECT",EDGE,{"disambiguationData":[OD(0.0)],"derivedFrom":[makeQuery(id+"F5.opExtrude","SWEPT_FACE",FACE,{"disambiguationData":[OSD([sQuery(id+"F4.wireOp",EDGE,"E30")])]}),makeQuery(id+"F8.opExtrude","SWEPT_FACE",FACE,{"disambiguationData":[OSD([sQuery(id+"F7.wireOp",EDGE,"E67")])]})]});
            fillet(context, id + "F14", {"entities" : qUnion([Q0, Q1, Q2, Q3, Q4, Q5]), "radius" : 3 * mm, "tangentPropagation" : true, "allowEdgeOverflow" : false});
        }
        {
            var Q0;
            Q0=makeQuery(id+"F1.opExtrude","CAP_EDGE",EDGE,{"disambiguationData":[OSD([sQuery(id+"F0.wireOp",EDGE,"E1.bottom")])],"isStart":false});
            fillet(context, id + "F15", {"entities" : qUnion([Q0]), "radius" : 2 * mm, "tangentPropagation" : true, "allowEdgeOverflow" : false});
        }
        {
            var Q0;
            {var subQ0=sQuery(id+"F0.wireOp",EDGE,"E22.filletArc");var subQ1=sQuery(id+"F0.wireOp",EDGE,"E7");var subQ2=sQuery(id+"F0.wireOp",EDGE,"E6");var subQ3=sQuery(id+"F0.wireOp",EDGE,"E5");var subQ4=sQuery(id+"F0.wireOp",EDGE,"E4");var subQ5=sQuery(id+"F0.wireOp",EDGE,"E1.bottom");var subQ6=sQuery(id+"F0.wireOp",EDGE,"E21.filletArc");var subQ7=sQuery(id+"F0.wireOp",EDGE,"E1.top");var subQ8=sQuery(id+"F0.wireOp",EDGE,"E1.left");var subQ9=sQuery(id+"F0.wireOp",EDGE,"E1.right");var subQ10=sQuery(id+"F0.wireOp",EDGE,"E23.filletArc");var subQ11=sQuery(id+"F0.wireOp",EDGE,"E24.filletArc");Q0=makeQuery(id+"F2.boolean.opBoolean","SPLIT",FACE,{"disambiguationData":[TD([makeQuery(id+"F1.opExtrude","SWEPT_FACE",FACE,{"disambiguationData":[OSD([subQ5])]})])],"derivedFrom":makeQuery(id+"F1.opExtrude","CAP_FACE",FACE,{"disambiguationData":[OSD([subQ5,subQ7,subQ8,subQ9,subQ4,subQ3,subQ2,subQ1,subQ6,subQ0,subQ10,subQ11])],"isStart":true})});}
            var sketch = newSketch(context, id + "F16", { "sketchPlane" : qUnion([Q0])});
            skLineSegment(sketch, "E79", {"start": v(0, 90) * mm, "end": v(0, 120) * mm, "construction": true});
            skLineSegment(sketch, "E80", {"start": v(-14.87, 108) * mm, "end": v(-14.87, 118.04) * mm});
            skCircle(sketch, "E81", {"center": v(0, 120) * mm, "radius": 6 * mm});
            skArc(sketch, "E82", {"start": v(14.87, 118.04) * mm, "mid": v(0, 135) * mm, "end": v(-14.87, 118.04) * mm});
            skLineSegment(sketch, "E83", {"start": v(14.87, 118.04) * mm, "end": v(14.87, 94.73) * mm});
            skLineSegment(sketch, "E84", {"start": v(14.87, 94.73) * mm, "end": v(19.6, 90) * mm});
            skLineSegment(sketch, "E85", {"start": v(-14.87, 108) * mm, "end": v(-32.87, 90) * mm});
            skLineSegment(sketch, "E86", {"start": v(-90, 0) * mm, "end": v(90, 0) * mm, "construction": true});
            skLineSegment(sketch, "E87.MirrorCS", {"start": v(-14.87, -108) * mm, "end": v(-32.87, -90) * mm});
            skLineSegment(sketch, "E88.MirrorCS", {"start": v(-14.87, -108) * mm, "end": v(-14.87, -118.04) * mm});
            skArc(sketch, "E89.MirrorCS", {"start": v(14.87, -118.04) * mm, "mid": v(0, -135) * mm, "end": v(-14.87, -118.04) * mm});
            skCircle(sketch, "E90.MirrorC", {"center": v(0, -120) * mm, "radius": 6 * mm});
            skLineSegment(sketch, "E91.MirrorCS", {"start": v(0, -90) * mm, "end": v(0, -120) * mm, "construction": true});
            skLineSegment(sketch, "E92.MirrorCS", {"start": v(14.87, -118.04) * mm, "end": v(14.87, -94.73) * mm});
            skLineSegment(sketch, "E93.MirrorCS", {"start": v(14.87, -94.73) * mm, "end": v(19.6, -90) * mm});
            skSolve(sketch);
        }
        {
            var Q0;
            {var subQ0=sQuery(id+"F16.wireOp",EDGE,"E87.MirrorCS");Q0=makeQuery(id+"F16.imprint","IMPRINT",FACE,{"disambiguationData":[TD([[makeQuery(id+"F16.imprint","IMPRINT",EDGE,{"derivedFrom":subQ0}),-1.0]])]});}
            var Q1;
            Q1=makeQuery(id+"F16.imprint","IMPRINT",FACE,{"disambiguationData":[TD([[makeQuery(id+"F16.imprint","IMPRINT",EDGE,{"derivedFrom":sQuery(id+"F16.wireOp",EDGE,"E80")}),-1.0]])]});
            var Q2;
            Q2=makeQuery(id+"F16.imprint","IMPRINT",FACE,{"disambiguationData":[TD([[makeQuery(id+"F16.imprint","IMPRINT",EDGE,{"derivedFrom":makeQuery(id+"F1.opExtrude","CAP_EDGE",EDGE,{"disambiguationData":[OSD([sQuery(id+"F0.wireOp",EDGE,"E1.left")])],"isStart":true})}),-1.0]])]});
            var Q3;
            Q3=makeQuery(id+"F2.opExtrude","CAP_FACE",FACE,{"disambiguationData":[OSD([sQuery(id+"F0.wireOp",EDGE,"E12"),sQuery(id+"F0.wireOp",EDGE,"E13"),sQuery(id+"F0.wireOp",EDGE,"E14"),sQuery(id+"F0.wireOp",EDGE,"E15"),sQuery(id+"F0.wireOp",EDGE,"E17.filletArc"),sQuery(id+"F0.wireOp",EDGE,"E18.filletArc"),sQuery(id+"F0.wireOp",EDGE,"E19.filletArc"),sQuery(id+"F0.wireOp",EDGE,"E20.filletArc"),sQuery(id+"F0.wireOp",EDGE,"E25.0"),sQuery(id+"F0.wireOp",EDGE,"E25.1"),sQuery(id+"F0.wireOp",EDGE,"E25.2"),sQuery(id+"F0.wireOp",EDGE,"E25.3"),sQuery(id+"F0.wireOp",EDGE,"E25.4"),sQuery(id+"F0.wireOp",EDGE,"E25.5"),sQuery(id+"F0.wireOp",EDGE,"E25.6"),sQuery(id+"F0.wireOp",EDGE,"E25.7")])],"isStart":false});
            extrude(context, id + "F17", {"entities" : qUnion([Q0, Q1, Q2]), "endBound" : BoundingType.UP_TO_SURFACE, "endBoundEntityFace" : qUnion([Q3]), "depth" : 25 * mm});
        }
    });
